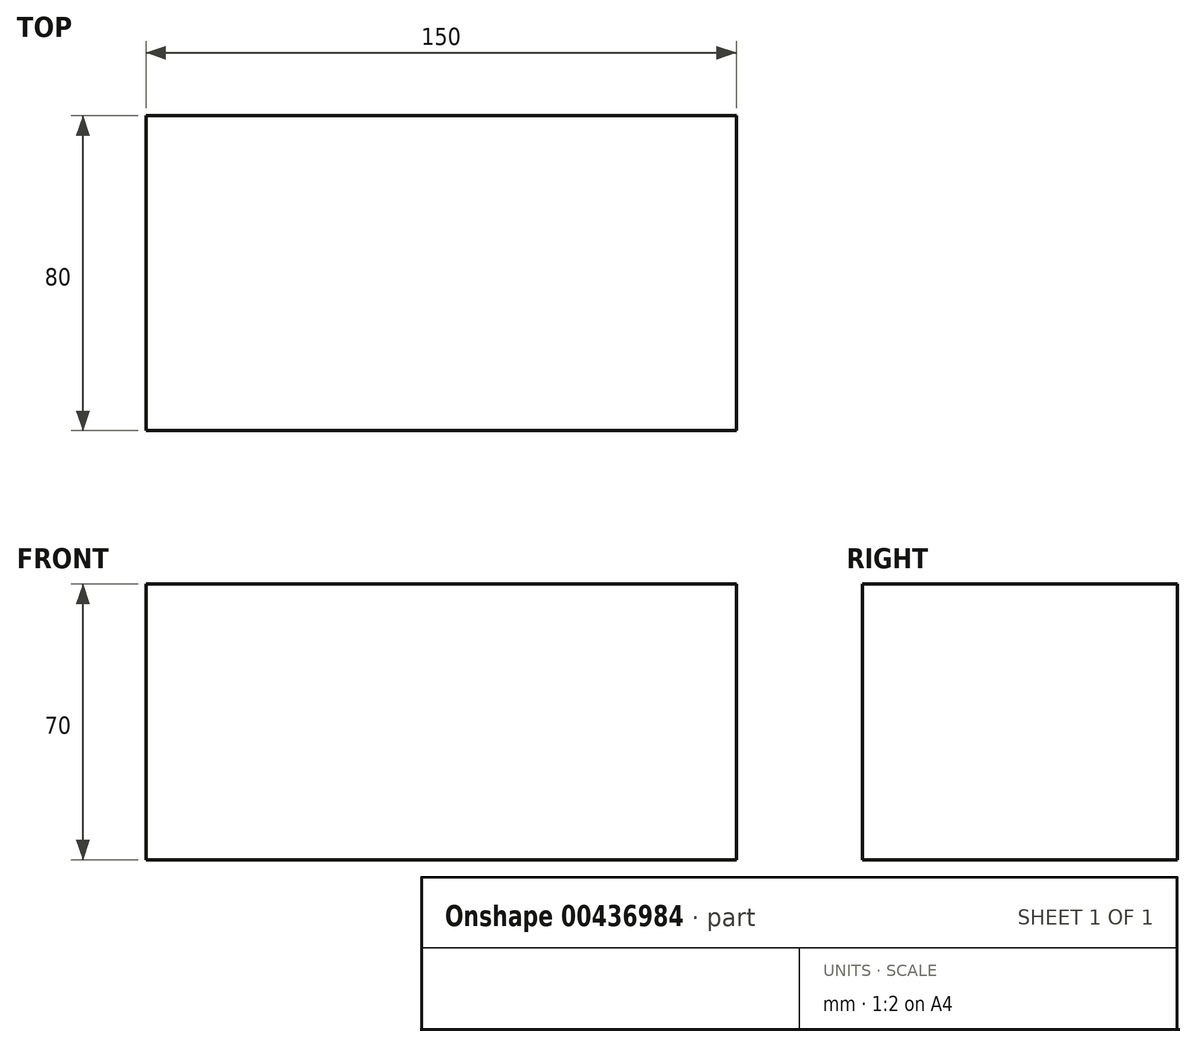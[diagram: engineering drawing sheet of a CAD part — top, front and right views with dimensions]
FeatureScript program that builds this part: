
annotation { "Feature Type Name" : "Feature", "Feature Type Description" : "" }
export const myFeature = defineFeature(function(context is Context, id is Id, definition is map)
    precondition{}
    {
        {
            var Q0;
            Q0=qCreatedBy(makeId("Top.planeOp"),FACE);
            var sketch = newSketch(context, id + "F0", { "sketchPlane" : qUnion([Q0])});
            skLineSegment(sketch, "E0.bottom", {"start": v(-75, 40) * mm, "end": v(75, 40) * mm});
            skLineSegment(sketch, "E0.top", {"start": v(-75, -40) * mm, "end": v(75, -40) * mm});
            skLineSegment(sketch, "E0.left", {"start": v(-75, 40) * mm, "end": v(-75, -40) * mm});
            skLineSegment(sketch, "E0.right", {"start": v(75, 40) * mm, "end": v(75, -40) * mm});
            skSolve(sketch);
        }
        {
            var Q0;
            Q0 = qSketchRegion(id + "F0", true);
            extrude(context, id + "F1", {"entities" : qUnion([Q0]), "depth" : 70 * mm});
        }
    });
